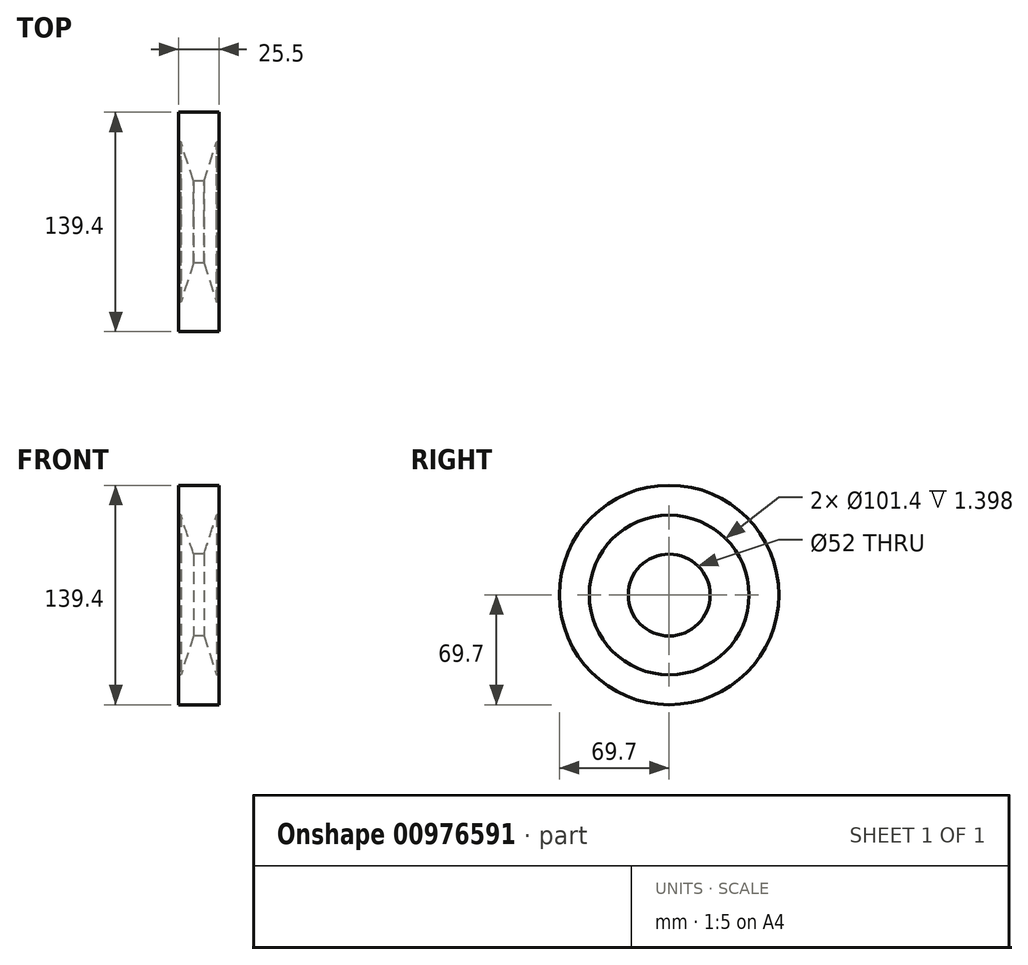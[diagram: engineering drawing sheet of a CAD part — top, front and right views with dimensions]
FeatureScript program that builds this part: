
annotation { "Feature Type Name" : "Feature", "Feature Type Description" : "" }
export const myFeature = defineFeature(function(context is Context, id is Id, definition is map)
    precondition{}
    {
        {
            var Q0;
            Q0=qCreatedBy(makeId("Front.planeOp"),FACE);
            var sketch = newSketch(context, id + "F0", { "sketchPlane" : qUnion([Q0])});
            skLineSegment(sketch, "E0", {"start": v(-3.33, 26) * mm, "end": v(3.33, 26) * mm});
            skLineSegment(sketch, "E1", {"start": v(3.33, 26) * mm, "end": v(11.35, 50.7) * mm});
            skLineSegment(sketch, "E2", {"start": v(12.75, 50.7) * mm, "end": v(11.35, 50.7) * mm});
            skLineSegment(sketch, "E3", {"start": v(0, 50.7) * mm, "end": v(0, 26) * mm, "construction": true});
            skLineSegment(sketch, "E4", {"start": v(-63.88, 0) * mm, "end": v(103.5, 0) * mm, "construction": true});
            skLineSegment(sketch, "E5", {"start": v(0, 45) * mm, "end": v(9.5, 45) * mm, "construction": true});
            skLineSegment(sketch, "E6.MirrorCS", {"start": v(-3.33, 26) * mm, "end": v(-11.35, 50.7) * mm});
            skLineSegment(sketch, "E7", {"start": v(12.75, 50.7) * mm, "end": v(12.75, 69.7) * mm});
            skLineSegment(sketch, "E8.MirrorCS", {"start": v(-12.75, 50.7) * mm, "end": v(-12.75, 69.7) * mm});
            skLineSegment(sketch, "E9", {"start": v(12.75, 69.7) * mm, "end": v(-12.75, 69.7) * mm});
            skLineSegment(sketch, "E10", {"start": v(-11.35, 50.7) * mm, "end": v(-12.75, 50.7) * mm});
            skSolve(sketch);
        }
        {
            var Q0;
            Q0=makeQuery(id+"F0.imprint","IMPRINT",FACE,{"disambiguationData":[TD([[makeQuery(id+"F0.imprint","IMPRINT",EDGE,{"derivedFrom":sQuery(id+"F0.wireOp",EDGE,"E0")}),1.0]])]});
            var Q1;
            Q1=sQuery(id+"F0.wireOp",EDGE,"E4");
            revolve(context, id + "F1", {"surfaceOperationType" : NewSurfaceOperationType.NEW, "entities" : qUnion([Q0]), "axis" : qUnion([Q1]), "revolveType" : RevolveType.FULL});
        }
    });
